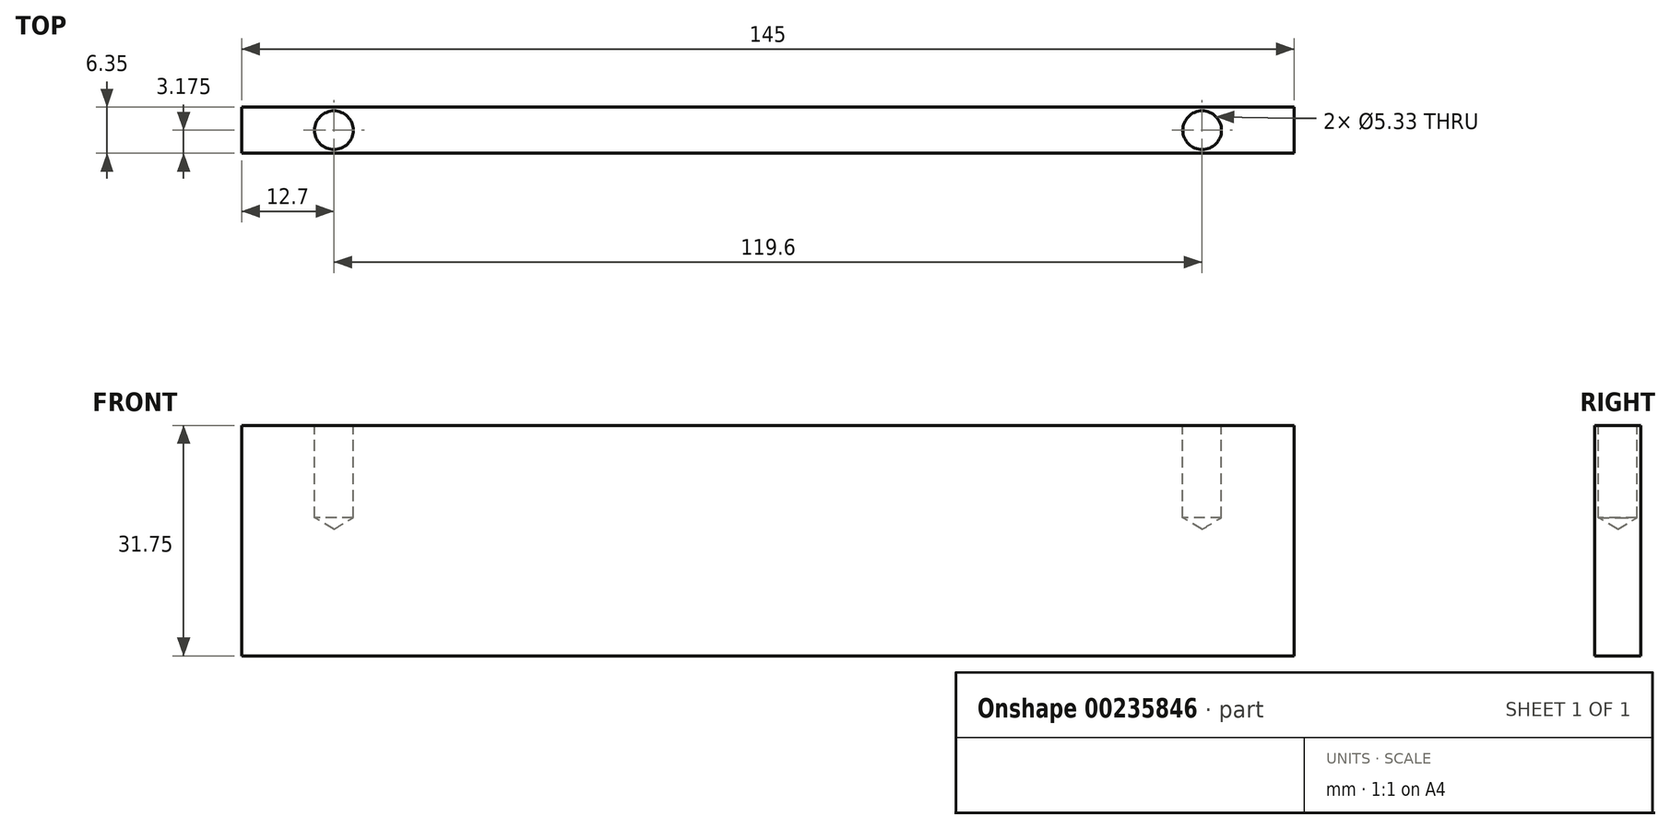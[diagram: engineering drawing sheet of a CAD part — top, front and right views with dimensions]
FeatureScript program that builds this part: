
annotation { "Feature Type Name" : "Feature", "Feature Type Description" : "" }
export const myFeature = defineFeature(function(context is Context, id is Id, definition is map)
    precondition{}
    {
        {
            var Q0;
            Q0=qCreatedBy(makeId("Front.planeOp"),FACE);
            var sketch = newSketch(context, id + "F0", { "sketchPlane" : qUnion([Q0])});
            skLineSegment(sketch, "E0.bottom", {"start": v(0, 0) * mm, "end": v(145, 0) * mm});
            skLineSegment(sketch, "E0.top", {"start": v(0, 31.75) * mm, "end": v(145, 31.75) * mm});
            skLineSegment(sketch, "E0.left", {"start": v(0, 0) * mm, "end": v(0, 31.75) * mm});
            skLineSegment(sketch, "E0.right", {"start": v(145, 0) * mm, "end": v(145, 31.75) * mm});
            skSolve(sketch);
        }
        {
            var Q0;
            Q0=makeQuery(id+"F0.imprint","IMPRINT",FACE,{"disambiguationData":[TD([[makeQuery(id+"F0.imprint","IMPRINT",EDGE,{"derivedFrom":sQuery(id+"F0.wireOp",EDGE,"E0.bottom")}),1.0]])]});
            extrude(context, id + "F1", {"entities" : qUnion([Q0]), "depth" : 6.35 * mm});
        }
        {
            var Q0;
            Q0=makeQuery(id+"F1.opExtrude","SWEPT_FACE",FACE,{"disambiguationData":[OSD([sQuery(id+"F0.wireOp",EDGE,"E0.top")])]});
            var sketch = newSketch(context, id + "F2", { "sketchPlane" : qUnion([Q0])});
            skPoint(sketch, "E1", {"position": v(12.7, -3.18) * mm});
            skPoint(sketch, "E2", {"position": v(132.3, -3.17) * mm});
            skSolve(sketch);
        }
        {
            var Q0;
            Q0=sQuery(id+"F2.wireOp",VERTEX,"E1");
            var Q1;
            Q1=sQuery(id+"F2.wireOp",VERTEX,"E2");
            var Q2;
            Q2=makeQuery(id+"F1.opExtrude","SWEPT_BODY",BODY,{"disambiguationData":[OSD([sQuery(id+"F0.wireOp",EDGE,"E0.bottom"),sQuery(id+"F0.wireOp",EDGE,"E0.top"),sQuery(id+"F0.wireOp",EDGE,"E0.left"),sQuery(id+"F0.wireOp",EDGE,"E0.right")])]});
            hole(context, id + "F3", {"style" : HoleStyle.SIMPLE, "endStyle" : HoleEndStyle.BLIND, "holeDiameter" : 5.33 * mm, "holeDepth" : 12.7 * mm, "locations" : qUnion([Q0, Q1]), "scope" : qUnion([Q2])});
        }
    });
